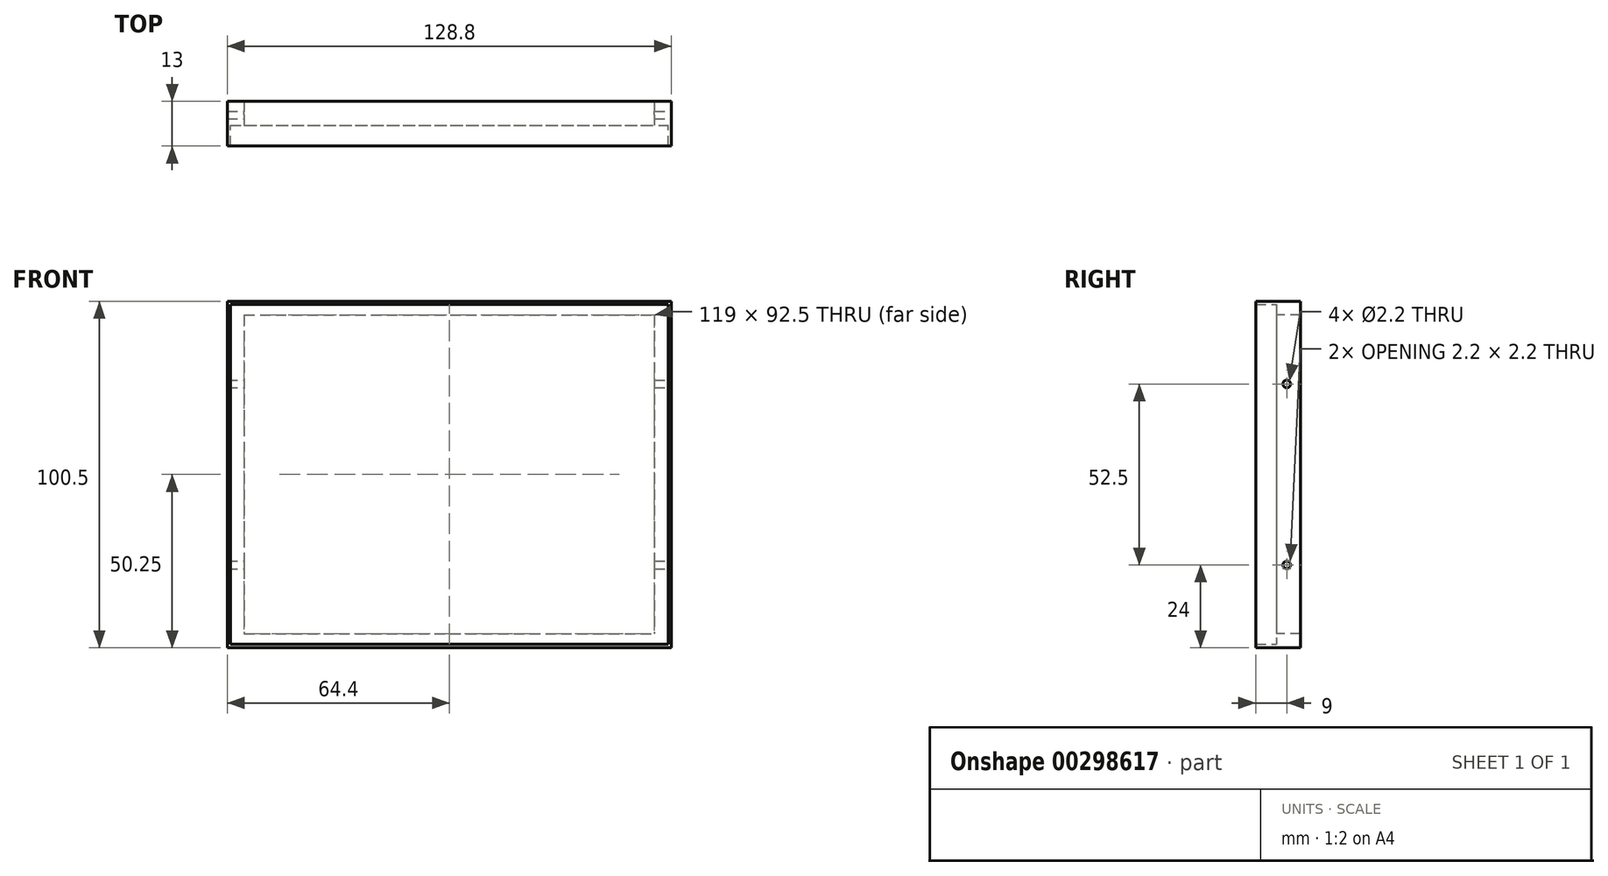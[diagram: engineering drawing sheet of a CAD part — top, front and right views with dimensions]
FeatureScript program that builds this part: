
annotation { "Feature Type Name" : "Feature", "Feature Type Description" : "" }
export const myFeature = defineFeature(function(context is Context, id is Id, definition is map)
    precondition{}
    {
        {
            var Q0;
            Q0=qCreatedBy(makeId("Front.planeOp"),FACE);
            var sketch = newSketch(context, id + "F0", { "sketchPlane" : qUnion([Q0])});
            skLineSegment(sketch, "E0.bottom", {"start": v(57.5, -43.25) * mm, "end": v(-57.5, -43.25) * mm});
            skLineSegment(sketch, "E0.top", {"start": v(57.5, 43.25) * mm, "end": v(-57.5, 43.25) * mm});
            skLineSegment(sketch, "E0.left", {"start": v(57.5, -43.25) * mm, "end": v(57.5, 43.25) * mm});
            skLineSegment(sketch, "E0.right", {"start": v(-57.5, -43.25) * mm, "end": v(-57.5, 43.25) * mm});
            skPoint(sketch, "E0.middle", {"position": v(0, 0) * mm});
            skLineSegment(sketch, "E1.bottom", {"start": v(-62.5, 46.25) * mm, "end": v(64.5, 46.25) * mm});
            skLineSegment(sketch, "E1.top", {"start": v(-62.5, -52.25) * mm, "end": v(64.5, -52.25) * mm});
            skLineSegment(sketch, "E1.left", {"start": v(-62.5, 46.25) * mm, "end": v(-62.5, -52.25) * mm});
            skLineSegment(sketch, "E1.right", {"start": v(64.5, 46.25) * mm, "end": v(64.5, -52.25) * mm});
            skSolve(sketch);
        }
        {
            var Q0;
            Q0=qCreatedBy(makeId("Front.planeOp"),FACE);
            var sketch = newSketch(context, id + "F1", { "sketchPlane" : qUnion([Q0])});
            skLineSegment(sketch, "E2.bottom", {"start": v(-62.5, 46.25) * mm, "end": v(64.5, 46.25) * mm});
            skLineSegment(sketch, "E2.top", {"start": v(-62.5, -52.25) * mm, "end": v(64.5, -52.25) * mm});
            skLineSegment(sketch, "E2.left", {"start": v(-62.5, 46.25) * mm, "end": v(-62.5, -52.25) * mm});
            skLineSegment(sketch, "E2.right", {"start": v(64.5, 46.25) * mm, "end": v(64.5, -52.25) * mm});
            skLineSegment(sketch, "E3.bottom", {"start": v(-63.4, 47.25) * mm, "end": v(65.4, 47.25) * mm});
            skLineSegment(sketch, "E3.top", {"start": v(-63.4, -53.25) * mm, "end": v(65.4, -53.25) * mm});
            skLineSegment(sketch, "E3.left", {"start": v(-63.4, 47.25) * mm, "end": v(-63.4, -53.25) * mm});
            skLineSegment(sketch, "E3.right", {"start": v(65.4, 47.25) * mm, "end": v(65.4, -53.25) * mm});
            skSolve(sketch);
        }
        {
            var Q0;
            Q0=qSketchRegion(id+"F1",true);
            extrude(context, id + "F2", {"entities" : qUnion([Q0]), "depth" : 6 * mm});
        }
        {
            var Q0;
            Q0=qCreatedBy(makeId("Front.planeOp"),FACE);
            var sketch = newSketch(context, id + "F3", { "sketchPlane" : qUnion([Q0])});
            skLineSegment(sketch, "E4.bottom", {"start": v(-63.4, 47.25) * mm, "end": v(65.4, 47.25) * mm});
            skLineSegment(sketch, "E4.top", {"start": v(-63.4, -53.25) * mm, "end": v(65.4, -53.25) * mm});
            skLineSegment(sketch, "E4.left", {"start": v(-63.4, 47.25) * mm, "end": v(-63.4, -53.25) * mm});
            skLineSegment(sketch, "E4.right", {"start": v(65.4, 47.25) * mm, "end": v(65.4, -53.25) * mm});
            skLineSegment(sketch, "E5.bottom", {"start": v(-58.5, 43.25) * mm, "end": v(60.5, 43.25) * mm});
            skLineSegment(sketch, "E5.top", {"start": v(-58.5, -49.25) * mm, "end": v(60.5, -49.25) * mm});
            skLineSegment(sketch, "E5.left", {"start": v(-58.5, 43.25) * mm, "end": v(-58.5, -49.25) * mm});
            skLineSegment(sketch, "E5.right", {"start": v(60.5, 43.25) * mm, "end": v(60.5, -49.25) * mm});
            skSolve(sketch);
        }
        {
            var Q0;
            Q0=qSketchRegion(id+"F3",true);
            extrude(context, id + "F4", {"entities" : qUnion([Q0]), "operationType" : NewBodyOperationType.ADD, "oppositeDirection" : true, "depth" : 7 * mm});
        }
        {
            var Q0;
            Q0=makeQuery(id+"F4.boolean.opBoolean","MERGE",FACE,{"derivedFrom":[makeQuery(id+"F2.opExtrude","SWEPT_FACE",FACE,{"disambiguationData":[OSD([sQuery(id+"F1.wireOp",EDGE,"E3.right")])]}),makeQuery(id+"F4.opExtrude","SWEPT_FACE",FACE,{"disambiguationData":[OSD([sQuery(id+"F3.wireOp",EDGE,"E4.right")])]})]});
            var sketch = newSketch(context, id + "F5", { "sketchPlane" : qUnion([Q0])});
            skCircle(sketch, "E6", {"center": v(3, -29.25) * mm, "radius": 1.1 * mm});
            skCircle(sketch, "E7", {"center": v(3, 23.25) * mm, "radius": 1.1 * mm});
            skSolve(sketch);
        }
        {
            var Q0;
            Q0 = qSketchRegion(id + "F5", true);
            extrude(context, id + "F6", {"entities" : qUnion([Q0]), "operationType" : NewBodyOperationType.REMOVE, "endBound" : BoundingType.THROUGH_ALL, "oppositeDirection" : true, "depth" : 25 * mm});
        }
        {
            var Q0;
            Q0=makeQuery(id+"F4.opExtrude","CAP_FACE",FACE,{"disambiguationData":[OSD([sQuery(id+"F3.wireOp",EDGE,"E4.bottom"),sQuery(id+"F3.wireOp",EDGE,"E4.top"),sQuery(id+"F3.wireOp",EDGE,"E4.left"),sQuery(id+"F3.wireOp",EDGE,"E4.right"),sQuery(id+"F3.wireOp",EDGE,"E5.bottom"),sQuery(id+"F3.wireOp",EDGE,"E5.top"),sQuery(id+"F3.wireOp",EDGE,"E5.left"),sQuery(id+"F3.wireOp",EDGE,"E5.right")])],"isStart":true});
            var sketch = newSketch(context, id + "F7", { "sketchPlane" : qUnion([Q0])});
            skLineSegment(sketch, "E8.bottom", {"start": v(-62.5, 46.25) * mm, "end": v(64.5, 46.25) * mm});
            skLineSegment(sketch, "E8.top", {"start": v(-62.5, -52.25) * mm, "end": v(64.5, -52.25) * mm});
            skLineSegment(sketch, "E8.left", {"start": v(-62.5, 46.25) * mm, "end": v(-62.5, -52.25) * mm});
            skLineSegment(sketch, "E8.right", {"start": v(64.5, 46.25) * mm, "end": v(64.5, -52.25) * mm});
            skSolve(sketch);
        }
        {
            var Q0;
            Q0 = qSketchRegion(id + "F7", true);
            extrude(context, id + "F8", {"entities" : qUnion([Q0]), "depth" : 6 * mm, "offsetDistance" : 25 * mm});
        }
    });
